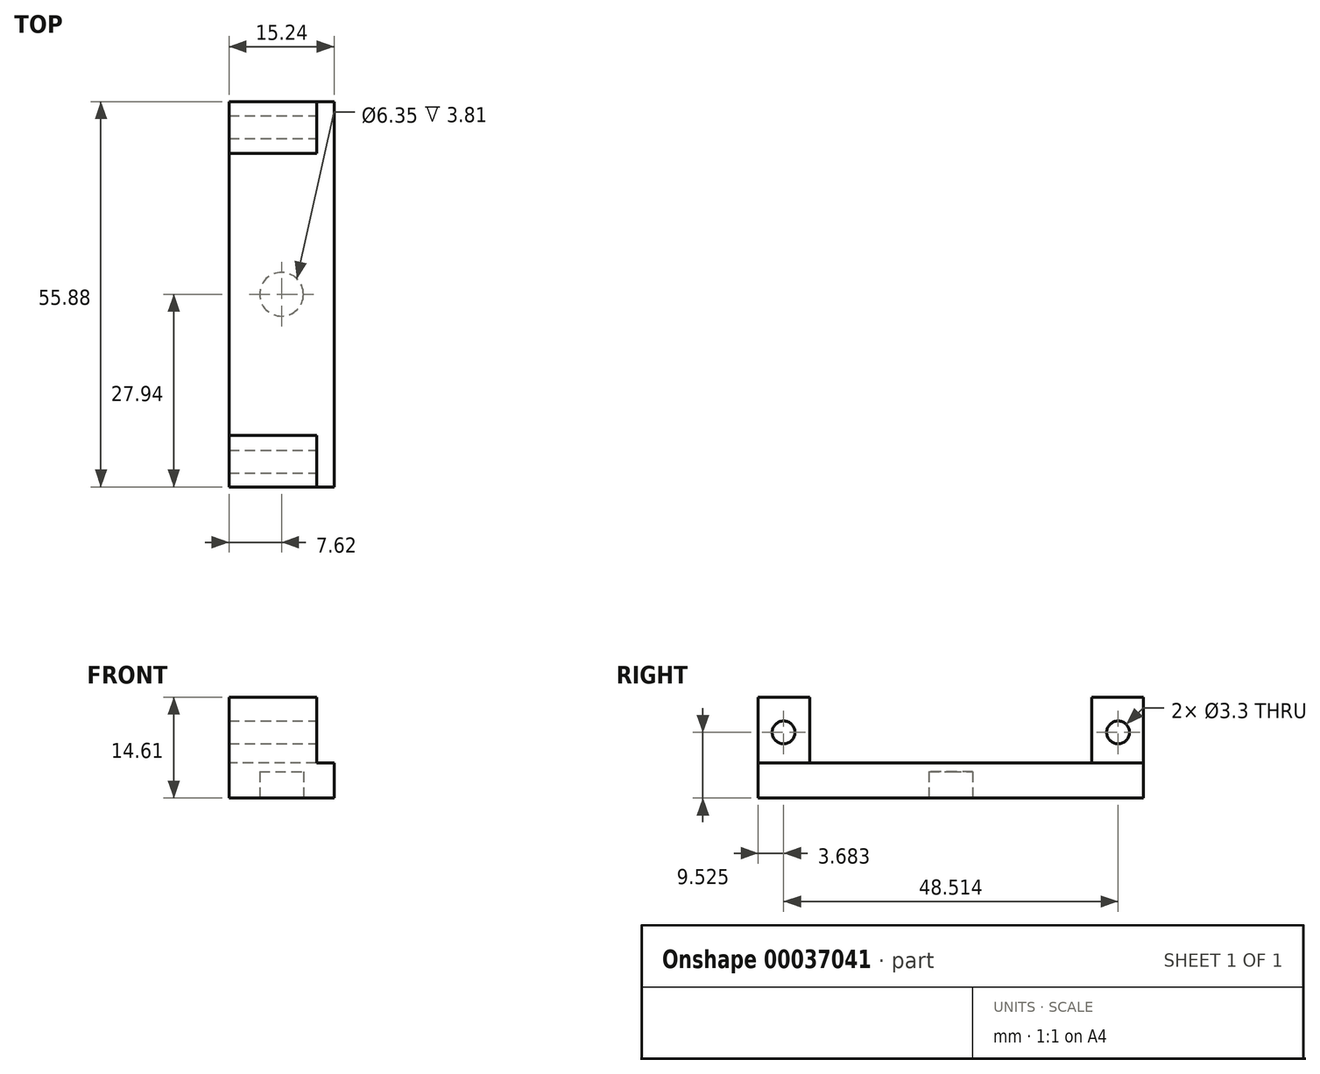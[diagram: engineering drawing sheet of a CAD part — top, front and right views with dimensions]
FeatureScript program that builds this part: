
annotation { "Feature Type Name" : "Feature", "Feature Type Description" : "" }
export const myFeature = defineFeature(function(context is Context, id is Id, definition is map)
    precondition{}
    {
        {
            var Q0;
            Q0=qCreatedBy(makeId("Right.planeOp"),FACE);
            var sketch = newSketch(context, id + "F0", { "sketchPlane" : qUnion([Q0])});
            skLineSegment(sketch, "E0", {"start": v(0, -5.08) * mm, "end": v(27.94, -5.08) * mm});
            skLineSegment(sketch, "E1", {"start": v(27.94, -5.08) * mm, "end": v(27.94, 9.53) * mm});
            skLineSegment(sketch, "E2", {"start": v(27.94, 9.53) * mm, "end": v(20.45, 9.53) * mm});
            skLineSegment(sketch, "E3", {"start": v(20.45, 9.53) * mm, "end": v(20.45, 0) * mm});
            skLineSegment(sketch, "E4", {"start": v(20.45, 0) * mm, "end": v(0, 0) * mm});
            skLineSegment(sketch, "E5", {"start": v(0, 0) * mm, "end": v(0, -5.08) * mm});
            skSolve(sketch);
        }
        {
            var Q0;
            Q0=qSketchRegion(id+"F0",true);
            extrude(context, id + "F1", {"entities" : qUnion([Q0]), "endBound" : BoundingType.SYMMETRIC, "depth" : 15.24 * mm});
        }
        {
            var Q0;
            Q0=makeQuery(id+"F1.opExtrude","SWEPT_BODY",BODY,{"disambiguationData":[OSD([sQuery(id+"F0.wireOp",EDGE,"E0"),sQuery(id+"F0.wireOp",EDGE,"E1"),sQuery(id+"F0.wireOp",EDGE,"E2"),sQuery(id+"F0.wireOp",EDGE,"E3"),sQuery(id+"F0.wireOp",EDGE,"E4"),sQuery(id+"F0.wireOp",EDGE,"E5")])]});
            var Q1;
            Q1=qCreatedBy(makeId("Front.planeOp"),FACE);
            mirror(context, id + "F2", {"operationType" : NewBodyOperationType.ADD, "entities" : qUnion([Q0]), "mirrorPlane" : qUnion([Q1])});
        }
        {
            var Q0;
            {var subQ0=makeQuery(id+"F1.opExtrude","CAP_FACE",FACE,{"disambiguationData":[OSD([sQuery(id+"F0.wireOp",EDGE,"E0"),sQuery(id+"F0.wireOp",EDGE,"E1"),sQuery(id+"F0.wireOp",EDGE,"E2"),sQuery(id+"F0.wireOp",EDGE,"E3"),sQuery(id+"F0.wireOp",EDGE,"E4"),sQuery(id+"F0.wireOp",EDGE,"E5")])],"isStart":false});Q0=makeQuery(id+"F2.boolean.opBoolean","MERGE",FACE,{"derivedFrom":[subQ0,makeQuery(id+"F2.opPattern","COPY",FACE,{"derivedFrom":subQ0,"instanceName":"1"})]});}
            var sketch = newSketch(context, id + "F3", { "sketchPlane" : qUnion([Q0])});
            skCircle(sketch, "E6", {"center": v(-24.26, 4.44) * mm, "radius": 1.65 * mm});
            skCircle(sketch, "E7", {"center": v(24.26, 4.45) * mm, "radius": 1.65 * mm});
            skLineSegment(sketch, "E8", {"start": v(24.26, 4.45) * mm, "end": v(-24.26, 4.44) * mm, "construction": true});
            skSolve(sketch);
        }
        {
            var Q0;
            Q0=qSketchRegion(id+"F3",true);
            extrude(context, id + "F4", {"entities" : qUnion([Q0]), "operationType" : NewBodyOperationType.REMOVE, "oppositeDirection" : true, "depth" : 25.4 * mm});
        }
        {
            var Q0;
            {var subQ0=makeQuery(id+"F1.opExtrude","SWEPT_FACE",FACE,{"disambiguationData":[OSD([sQuery(id+"F0.wireOp",EDGE,"E0")])]});Q0=makeQuery(id+"F2.boolean.opBoolean","MERGE",FACE,{"derivedFrom":[subQ0,makeQuery(id+"F2.opPattern","COPY",FACE,{"derivedFrom":subQ0,"instanceName":"1"})]});}
            var sketch = newSketch(context, id + "F5", { "sketchPlane" : qUnion([Q0])});
            skPoint(sketch, "E9", {"position": v(0, 0) * mm});
            skCircle(sketch, "E10", {"center": v(0, 0) * mm, "radius": 3.18 * mm});
            skSolve(sketch);
        }
        {
            var Q0;
            Q0=makeQuery(id+"F5.imprint","IMPRINT",FACE,{"disambiguationData":[TD([[makeQuery(id+"F5.imprint","IMPRINT",EDGE,{"derivedFrom":sQuery(id+"F5.wireOp",EDGE,"E10")}),1.0]])]});
            extrude(context, id + "F6", {"entities" : qUnion([Q0]), "operationType" : NewBodyOperationType.REMOVE, "oppositeDirection" : true, "depth" : 3.8 * mm});
        }
        {
            var Q0;
            {var subQ0=makeQuery(id+"F1.opExtrude","CAP_FACE",FACE,{"disambiguationData":[OSD([sQuery(id+"F0.wireOp",EDGE,"E0"),sQuery(id+"F0.wireOp",EDGE,"E1"),sQuery(id+"F0.wireOp",EDGE,"E2"),sQuery(id+"F0.wireOp",EDGE,"E3"),sQuery(id+"F0.wireOp",EDGE,"E4"),sQuery(id+"F0.wireOp",EDGE,"E5")])],"isStart":false});Q0=makeQuery(id+"F2.boolean.opBoolean","MERGE",FACE,{"derivedFrom":[subQ0,makeQuery(id+"F2.opPattern","COPY",FACE,{"derivedFrom":subQ0,"instanceName":"1"})]});}
            var sketch = newSketch(context, id + "F7", { "sketchPlane" : qUnion([Q0])});
            skLineSegment(sketch, "E11.bottom", {"start": v(-27.94, 9.53) * mm, "end": v(27.94, 9.53) * mm});
            skLineSegment(sketch, "E11.top", {"start": v(-27.94, 0) * mm, "end": v(27.94, 0) * mm});
            skLineSegment(sketch, "E11.left", {"start": v(-27.94, 9.53) * mm, "end": v(-27.94, 0) * mm});
            skLineSegment(sketch, "E11.right", {"start": v(27.94, 9.53) * mm, "end": v(27.94, 0) * mm});
            skSolve(sketch);
        }
        {
            var Q0;
            Q0=qSketchRegion(id+"F7",true);
            extrude(context, id + "F8", {"entities" : qUnion([Q0]), "operationType" : NewBodyOperationType.REMOVE, "oppositeDirection" : true, "depth" : 2.54 * mm});
        }
    });
